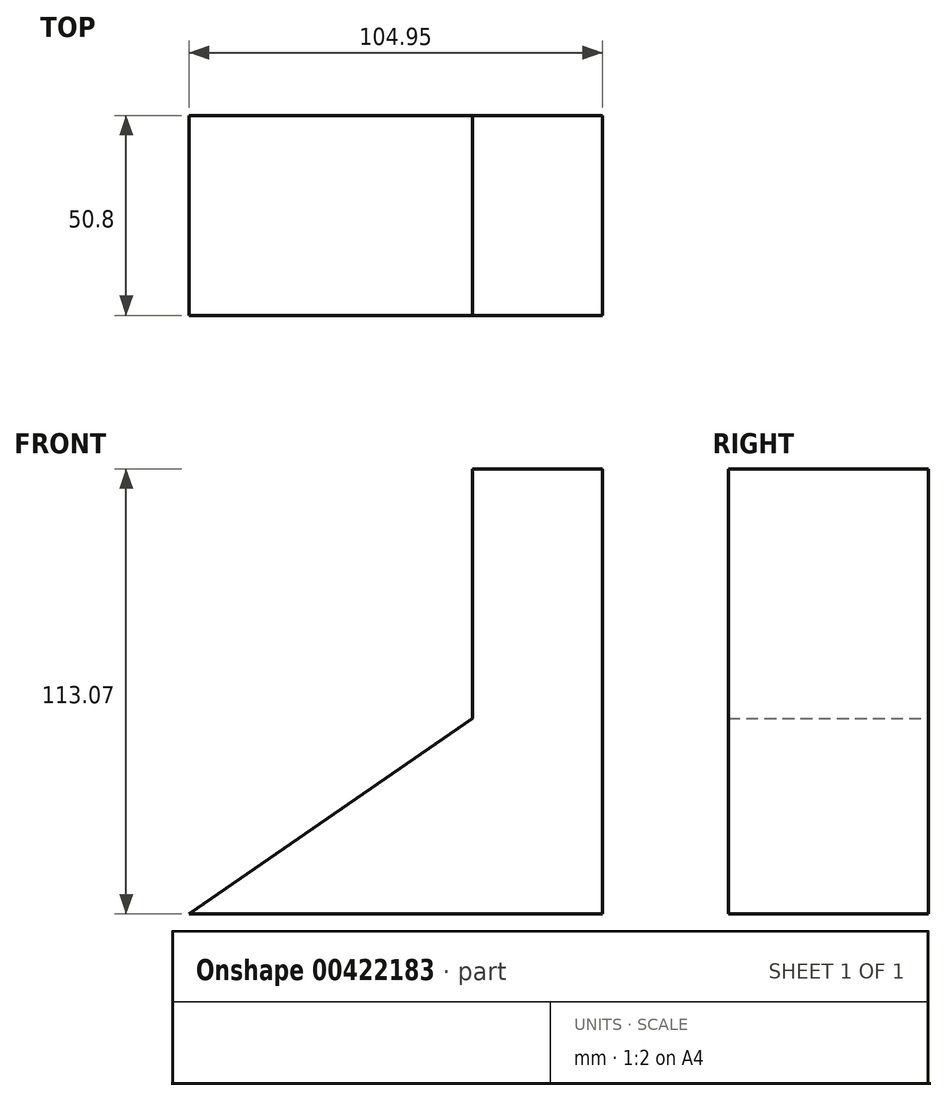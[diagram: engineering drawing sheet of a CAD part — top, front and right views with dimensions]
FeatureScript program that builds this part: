
annotation { "Feature Type Name" : "Feature", "Feature Type Description" : "" }
export const myFeature = defineFeature(function(context is Context, id is Id, definition is map)
    precondition{}
    {
        {
            var Q0;
            Q0=qCreatedBy(makeId("Front.planeOp"),FACE);
            var sketch = newSketch(context, id + "F0", { "sketchPlane" : qUnion([Q0])});
            skLineSegment(sketch, "E0", {"start": v(49.2, 57.44) * mm, "end": v(49.2, -55.63) * mm});
            skLineSegment(sketch, "E1", {"start": v(49.2, -55.63) * mm, "end": v(-55.75, -55.63) * mm});
            skLineSegment(sketch, "E2", {"start": v(-55.75, -55.63) * mm, "end": v(16.25, -5.98) * mm});
            skLineSegment(sketch, "E3", {"start": v(16.25, -5.98) * mm, "end": v(16.25, 55.18) * mm});
            skLineSegment(sketch, "E4", {"start": v(16.25, 55.18) * mm, "end": v(16.25, 57.44) * mm});
            skLineSegment(sketch, "E5", {"start": v(16.25, 57.44) * mm, "end": v(49.2, 57.44) * mm});
            skSolve(sketch);
        }
        {
            var Q0;
            Q0 = qSketchRegion(id + "F0", true);
            extrude(context, id + "F1", {"entities" : qUnion([Q0]), "depth" : 50.8 * mm});
        }
    });
